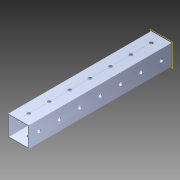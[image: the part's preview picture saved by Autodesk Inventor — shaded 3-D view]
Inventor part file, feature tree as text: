
AUTODESK INVENTOR PART (.ipt)
format: ipt  version: 2014 (Build 180170000, 170)  size: 1,150,464 bytes
history: native  units: in
note: dims shown in document units (in); Inventor stores cm internally (conversion verified against a paired STEP export)
features: pattern_circular x1, other x1, plane x1, extrude x1, imported_body x1, sketch x1
ambient origin geometry x8: Origin, YZ Plane, XZ Plane, XY Plane, X Axis, Y Axis, Z Axis, Center Point
bodies: Body1 (feature_tree)
feature tree (6):
  pattern_circular  "CirPattern2"
  other  "217-3426-STEP1"
  plane  "Work Plane1"
  extrude  "Extrusion1"  Depth=3937.0079in TaperAngle=0.0deg
  imported_body  "Base1"
  sketch  "Sketch1"  dims[d0=-7.0in d1=3937.0079in d2=0.0in]
